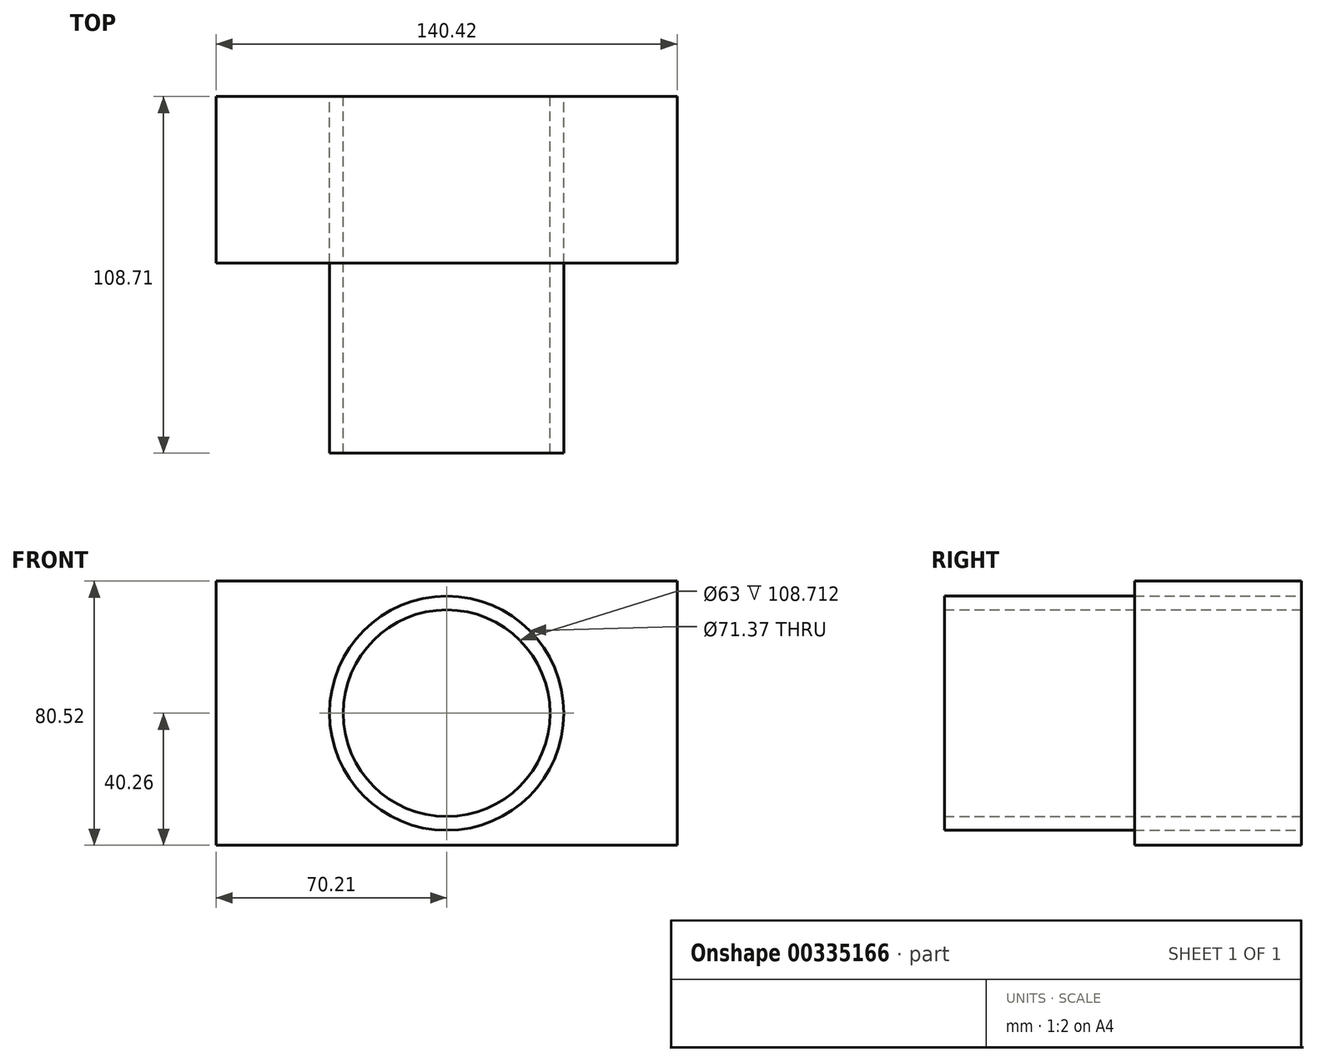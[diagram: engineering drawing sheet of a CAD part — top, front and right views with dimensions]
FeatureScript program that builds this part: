
annotation { "Feature Type Name" : "Feature", "Feature Type Description" : "" }
export const myFeature = defineFeature(function(context is Context, id is Id, definition is map)
    precondition{}
    {
        {
            var Q0;
            Q0=qCreatedBy(makeId("Front.planeOp"),FACE);
            var sketch = newSketch(context, id + "F0", { "sketchPlane" : qUnion([Q0])});
            skLineSegment(sketch, "E0.bottom", {"start": v(70.2, -40.26) * mm, "end": v(-70.2, -40.26) * mm});
            skLineSegment(sketch, "E0.top", {"start": v(70.2, 40.26) * mm, "end": v(-70.2, 40.26) * mm});
            skLineSegment(sketch, "E0.left", {"start": v(70.2, -40.26) * mm, "end": v(70.2, 40.26) * mm});
            skLineSegment(sketch, "E0.right", {"start": v(-70.2, -40.26) * mm, "end": v(-70.2, 40.26) * mm});
            skPoint(sketch, "E0.middle", {"position": v(0, 0) * mm});
            skCircle(sketch, "E1", {"center": v(0, 0) * mm, "radius": 35.69 * mm});
            skCircle(sketch, "E2", {"center": v(0, 0) * mm, "radius": 31.5 * mm});
            skSolve(sketch);
        }
        {
            var Q0;
            Q0=makeQuery(id+"F0.imprint","IMPRINT",FACE,{"disambiguationData":[TD([[makeQuery(id+"F0.imprint","IMPRINT",EDGE,{"derivedFrom":sQuery(id+"F0.wireOp",EDGE,"E0.bottom")}),-1.0]])]});
            extrude(context, id + "F1", {"entities" : qUnion([Q0]), "depth" : 50.8 * mm});
        }
        {
            var Q0;
            Q0=makeQuery(id+"F0.imprint","IMPRINT",FACE,{"disambiguationData":[TD([[makeQuery(id+"F0.imprint","IMPRINT",EDGE,{"derivedFrom":sQuery(id+"F0.wireOp",EDGE,"E1")}),1.0]])]});
            extrude(context, id + "F2", {"entities" : qUnion([Q0]), "depth" : 108.7 * mm});
        }
    });
